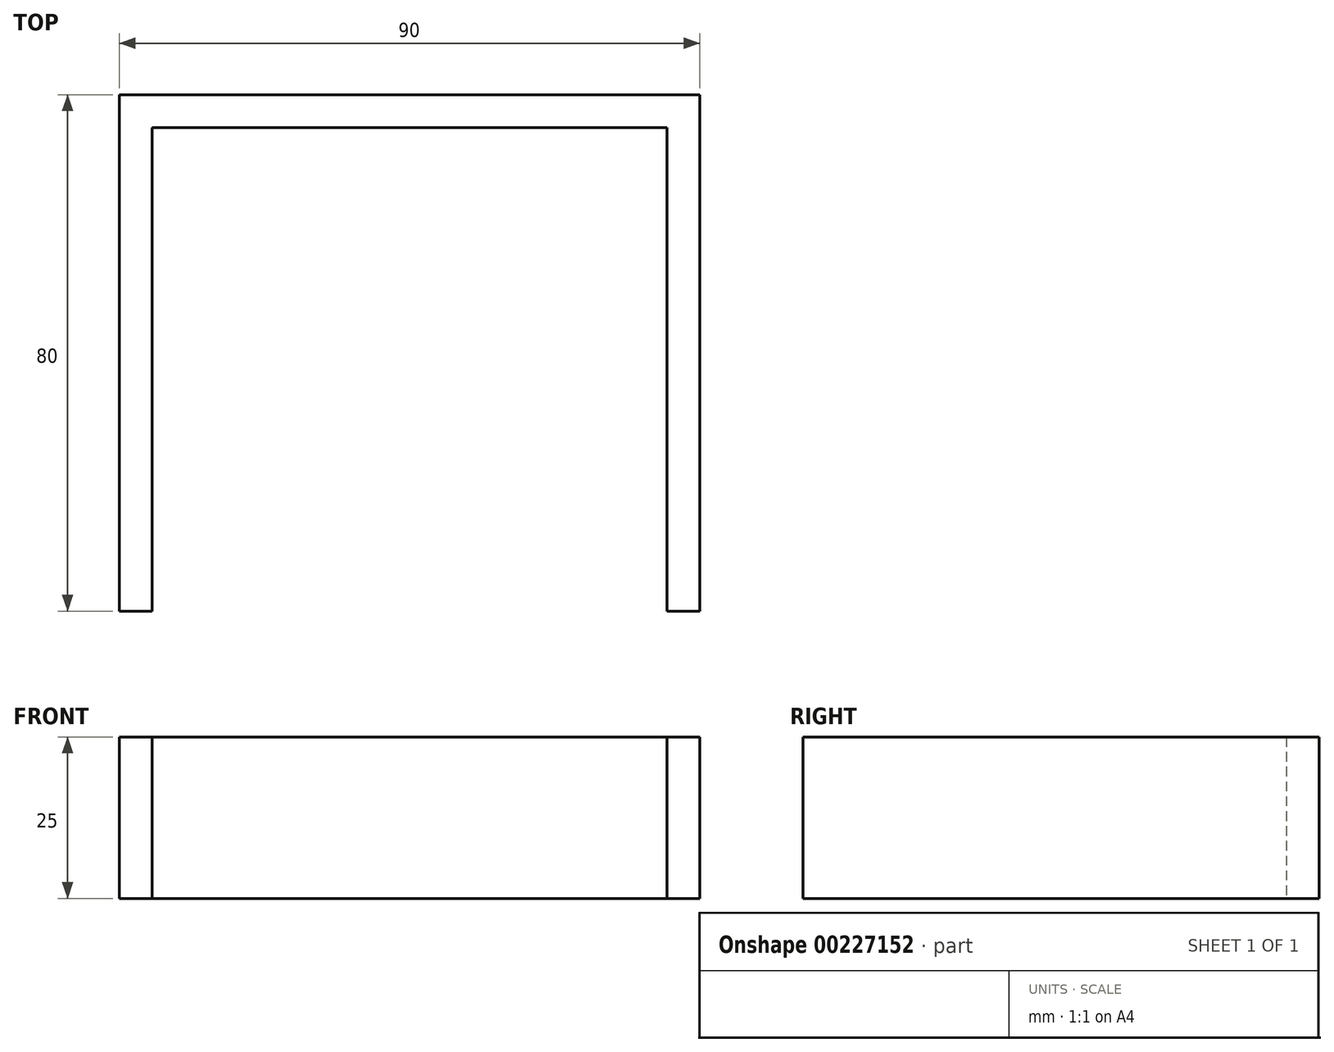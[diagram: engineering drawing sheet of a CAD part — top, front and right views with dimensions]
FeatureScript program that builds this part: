
annotation { "Feature Type Name" : "Feature", "Feature Type Description" : "" }
export const myFeature = defineFeature(function(context is Context, id is Id, definition is map)
    precondition{}
    {
        {
            var Q0;
            Q0=qCreatedBy(makeId("Top.planeOp"),FACE);
            var sketch = newSketch(context, id + "F0", { "sketchPlane" : qUnion([Q0])});
            skLineSegment(sketch, "E0.bottom", {"start": v(-109.1, 62.97) * mm, "end": v(-19.1, 62.97) * mm});
            skLineSegment(sketch, "E0.top", {"start": v(-109.1, -17.03) * mm, "end": v(-19.1, -17.03) * mm});
            skLineSegment(sketch, "E0.left", {"start": v(-109.1, 62.97) * mm, "end": v(-109.1, -17.03) * mm});
            skLineSegment(sketch, "E0.right", {"start": v(-19.1, 62.97) * mm, "end": v(-19.1, -17.03) * mm});
            skLineSegment(sketch, "E1.bottom", {"start": v(-104.02, -17.03) * mm, "end": v(-24.18, -17.03) * mm});
            skLineSegment(sketch, "E1.top", {"start": v(-104.02, 57.89) * mm, "end": v(-24.18, 57.89) * mm});
            skLineSegment(sketch, "E1.left", {"start": v(-104.02, -17.03) * mm, "end": v(-104.02, 57.89) * mm});
            skLineSegment(sketch, "E1.right", {"start": v(-24.18, -17.03) * mm, "end": v(-24.18, 57.89) * mm});
            skSolve(sketch);
        }
        {
            var Q0;
            Q0=makeQuery(id+"F0.imprint","IMPRINT",FACE,{"disambiguationData":[TD([[makeQuery(id+"F0.imprint","IMPRINT",EDGE,{"derivedFrom":sQuery(id+"F0.wireOp",EDGE,"E0.bottom")}),-1.0]])]});
            extrude(context, id + "F1", {"entities" : qUnion([Q0]), "depth" : 25 * mm, "offsetDistance" : 25 * mm});
        }
    });
